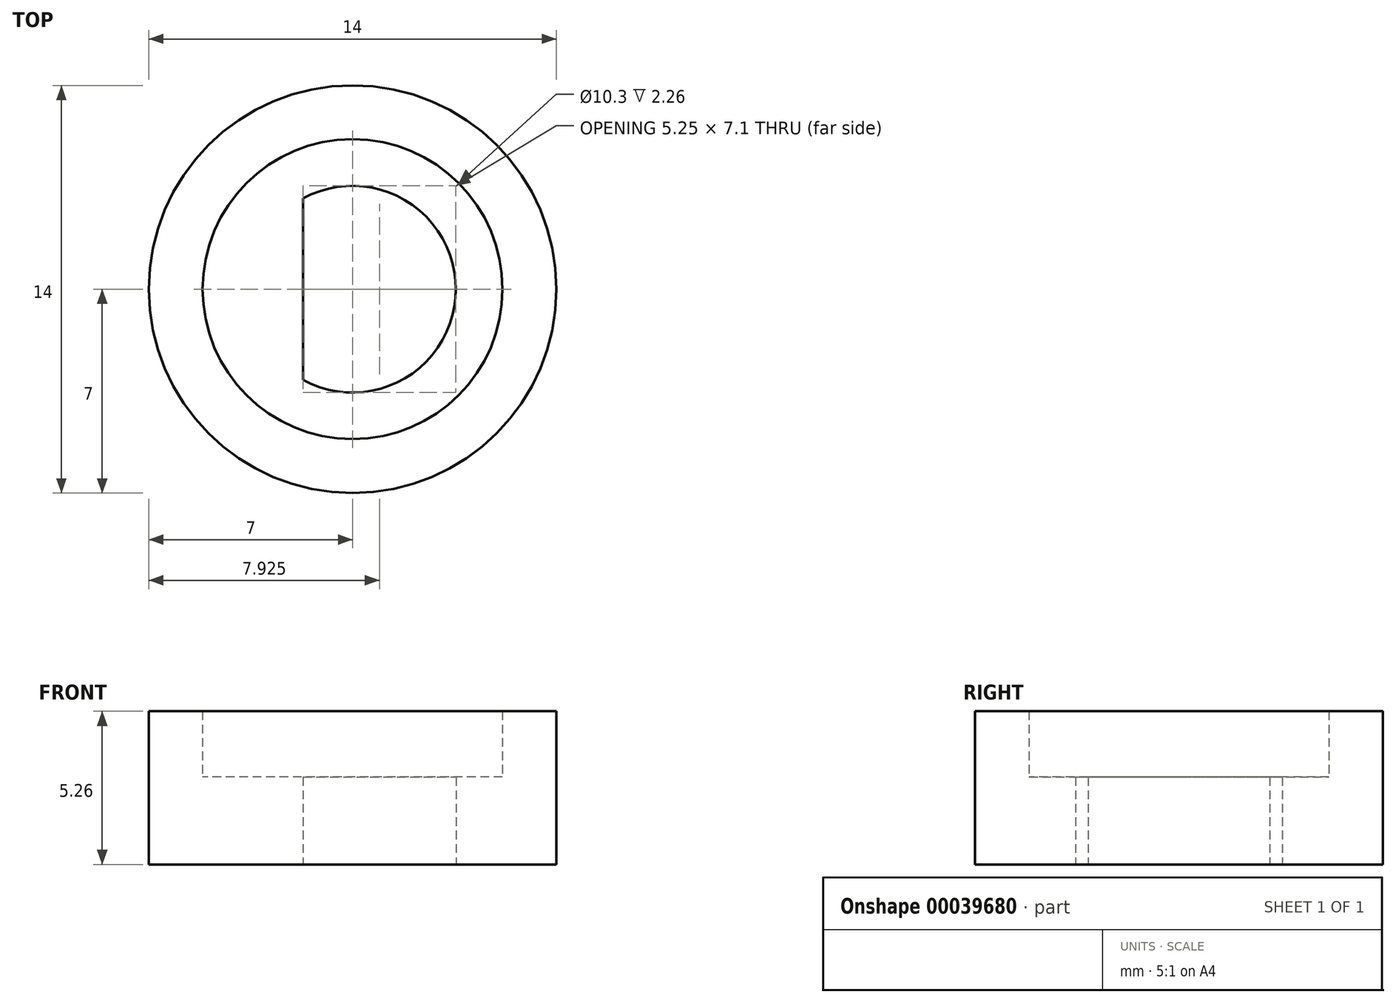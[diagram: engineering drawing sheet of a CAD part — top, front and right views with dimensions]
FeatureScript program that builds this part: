
annotation { "Feature Type Name" : "Feature", "Feature Type Description" : "" }
export const myFeature = defineFeature(function(context is Context, id is Id, definition is map)
    precondition{}
    {
        {
            var Q0;
            Q0=qCreatedBy(makeId("Top.planeOp"),FACE);
            var sketch = newSketch(context, id + "F0", { "sketchPlane" : qUnion([Q0])});
            skArc(sketch, "E0", {"start": v(-1.7, -3.12) * mm, "mid": v(3.55, 0) * mm, "end": v(-1.7, 3.12) * mm});
            skLineSegment(sketch, "E1", {"start": v(-1.7, 3.12) * mm, "end": v(-1.7, -3.12) * mm});
            skCircle(sketch, "E2", {"center": v(0, 0) * mm, "radius": 5.15 * mm});
            skCircle(sketch, "E3", {"center": v(0, 0) * mm, "radius": 7 * mm});
            skSolve(sketch);
        }
        {
            var Q0;
            Q0=makeQuery(id+"F0.imprint","IMPRINT",FACE,{"disambiguationData":[TD([[makeQuery(id+"F0.imprint","IMPRINT",EDGE,{"derivedFrom":sQuery(id+"F0.wireOp",EDGE,"E0")}),-1.0]])]});
            extrude(context, id + "F1", {"entities" : qUnion([Q0]), "depth" : 3 * mm});
        }
        {
            var Q0;
            Q0=makeQuery(id+"F0.imprint","IMPRINT",FACE,{"disambiguationData":[TD([[makeQuery(id+"F0.imprint","IMPRINT",EDGE,{"derivedFrom":sQuery(id+"F0.wireOp",EDGE,"E2")}),-1.0]])]});
            extrude(context, id + "F2", {"entities" : qUnion([Q0]), "operationType" : NewBodyOperationType.ADD, "depth" : 5.26 * mm});
        }
    });
